# Revit family: Enave P 180_240_Ukr 1
name_source: partatom
category: Оборудование
units: mm (PartAtom-declared; Revit-internal decimal feet)

## family parameters
Всегда вертикально = Да
Классификация = Нет
На основе рабочей плоскости = Нет
Общий = Нет
При загрузке вырезать с полостями = Нет
Размер круглого соединителя = Использовать диаметр
Тип детали = Нормальный
Точка принадлежности помещению = Нет

## types (4) — shared parameters
00_20_Виробник = Вентс
00_20_Назва = Припливно-витяжна установка
D = 160 мм
H = 290 мм
L = 1060 мм
Lk = 930 мм
W = 677 мм
Wk = 640 мм
d = 150 мм
wd1 = 134 мм
wd2 = 300 мм
Висота = 290 мм
Довжина = 1060 мм
Діаметр = 160 мм
Изготовитель = Вентс
Класифікація навантаження = HVAC
Кількість фаз = 1
Матеріал зони обслуговуваня = <По категории>
Матеріал корпусу = Полипропилен (черный)
Напруга = 230 В
Температура повітря, що переміщається = +45°С
Фільтр = Coarse > 60%
Ширина = 677 мм
zero-valued in all types: Отметка по умолчанию

## per-type parameters (varying)
| type | Вага | Максимальний потік повітря | Потужність | Рівень звукового тиску на відстані 3 м | Струм |
| Enave 180 P | 12.00 кг | 181.0 м³/ч | 53 Вт | 29 dBA | 0.490 А |
| Enave-T 180 P | 15.00 кг | 181.0 м³/ч | 53 Вт | 29 дБА | 0.490 А |
| Enave 240 P | 12.00 кг | 310.0 м³/ч | 171 Вт | 33 dBA | 1.340 А |
| Enave-T 240 P | 15.00 кг | 310.0 м³/ч | 171 Вт | 33 dBA | 1.340 А |

note: column(s) folded — value = type name in every type: 00_20_Тип
